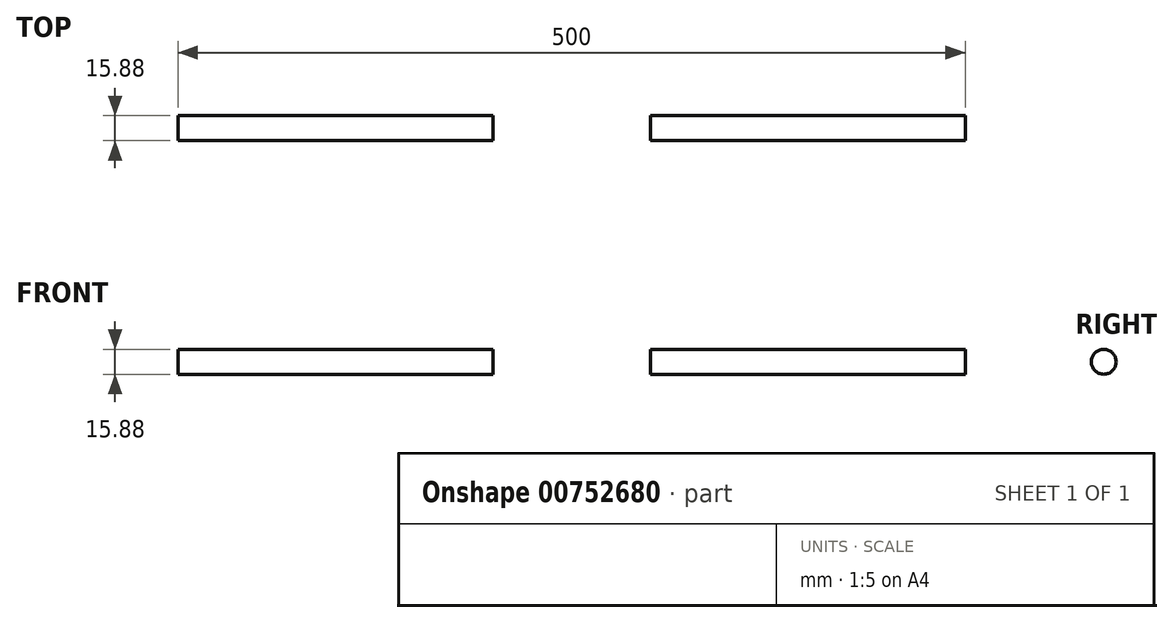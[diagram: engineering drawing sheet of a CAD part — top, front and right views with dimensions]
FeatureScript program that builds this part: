
annotation { "Feature Type Name" : "Feature", "Feature Type Description" : "" }
export const myFeature = defineFeature(function(context is Context, id is Id, definition is map)
    precondition{}
    {
        {
            var Q0;
            Q0=qCreatedBy(makeId("Right.planeOp"),FACE);
            var sketch = newSketch(context, id + "F0", { "sketchPlane" : qUnion([Q0])});
            skCircle(sketch, "E0", {"center": v(0, 0) * mm, "radius": 7.94 * mm});
            skSolve(sketch);
        }
        {
            var Q0;
            Q0 = qSketchRegion(id + "F0", true);
            extrude(context, id + "F1", {"entities" : qUnion([Q0]), "depth" : 200 * mm, "offsetDistance" : 25 * mm});
        }
        {
            var Q0;
            Q0 = qSketchRegion(id + "F0", true);
            extrude(context, id + "F2", {"entities" : qUnion([Q0]), "oppositeDirection" : true, "depth" : 200 * mm, "offsetDistance" : 25 * mm});
        }
        {
            var Q0;
            Q0=makeQuery(id+"F2.opExtrude","SWEPT_BODY",BODY,{"disambiguationData":[OSD([sQuery(id+"F0.wireOp",EDGE,"E0")])]});
            transform(context, id + "F3", {"entities" : qUnion([Q0]), "transformType" : TransformType.TRANSLATION_3D, "dx" : -50 * mm, "dy" : 0 * mm, "dz" : 0 * mm, "makeCopy" : false});
        }
        {
            var Q0;
            Q0=makeQuery(id+"F1.opExtrude","SWEPT_BODY",BODY,{"disambiguationData":[OSD([sQuery(id+"F0.wireOp",EDGE,"E0")])]});
            transform(context, id + "F4", {"entities" : qUnion([Q0]), "transformType" : TransformType.TRANSLATION_3D, "dx" : 50 * mm, "dy" : 0 * mm, "dz" : 0 * mm, "makeCopy" : false});
        }
    });
